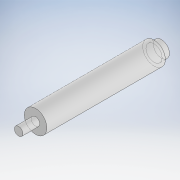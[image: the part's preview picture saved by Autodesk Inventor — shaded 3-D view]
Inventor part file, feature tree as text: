
AUTODESK INVENTOR PART (.ipt)
format: ipt  version: 2018.2 (Build 222227000, 227)  size: 102,912 bytes
history: native  units: mm
features: revolve x1, sketch x1
ambient origin geometry x8: Origin, YZ Plane, XZ Plane, XY Plane, X Axis, Y Axis, Z Axis, Center Point
bodies: Solid1 (feature_tree)
feature tree (2):
  revolve  "Revolution1"  [1 undecoded]
  sketch  "Sketch1"  dims[d0=3.0mm d1=6.0mm d2=50.5mm d3=5.7mm d4=8.0mm d5=2.6mm d6=90.0deg]
note: 1 required parameter value undecoded (feature->parameter linkage not recoverable at this tier; creation-order binding heuristic only, values carry confidence <= 0.55)
